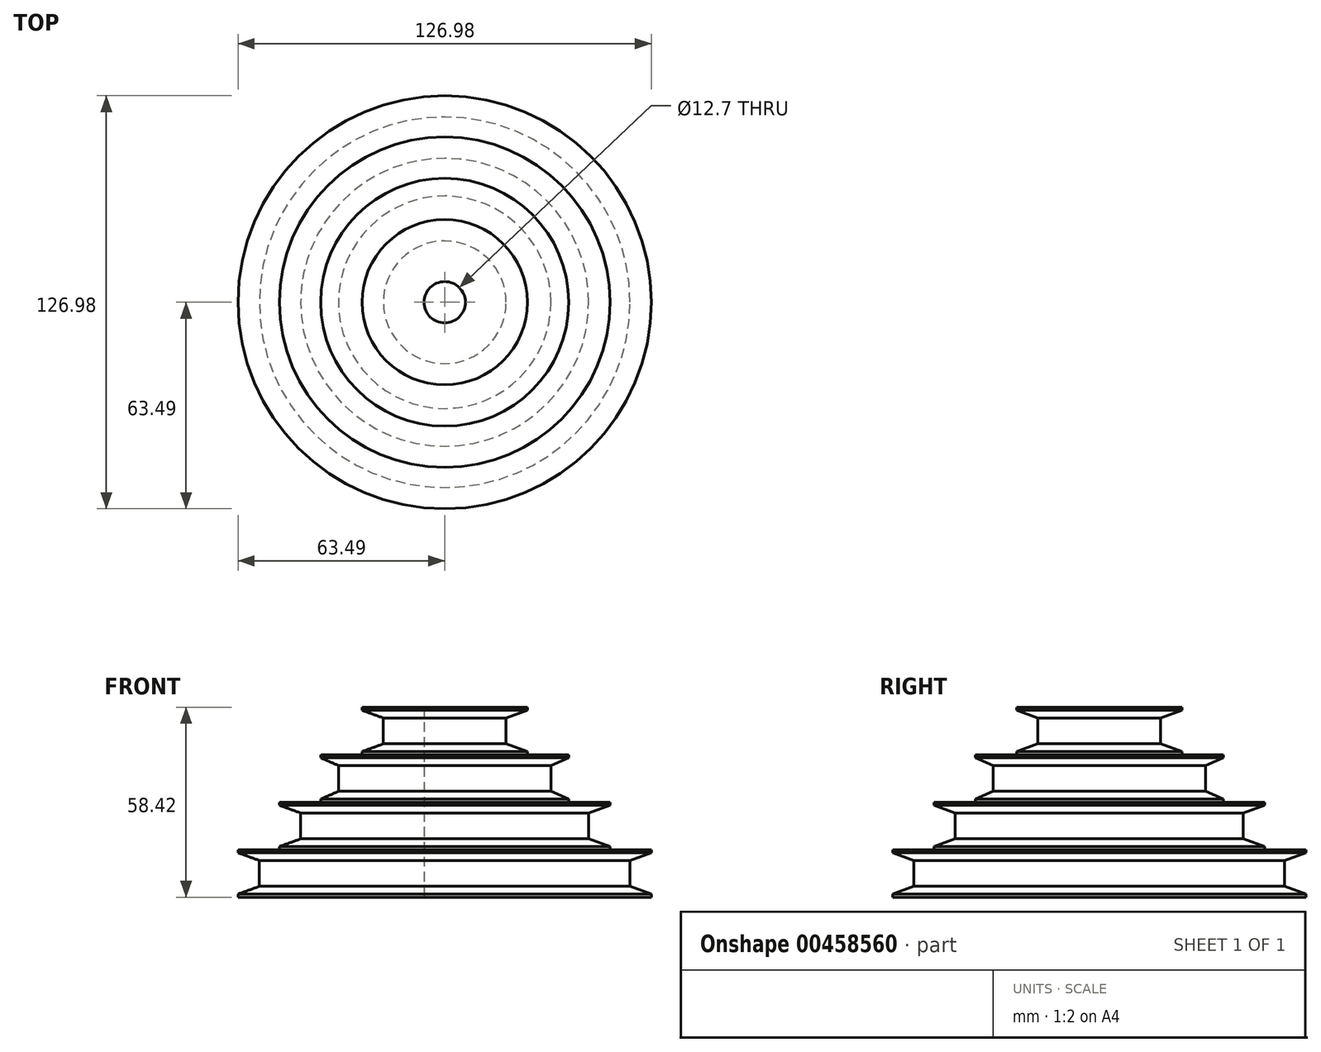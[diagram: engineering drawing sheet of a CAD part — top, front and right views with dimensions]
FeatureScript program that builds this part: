
annotation { "Feature Type Name" : "Feature", "Feature Type Description" : "" }
export const myFeature = defineFeature(function(context is Context, id is Id, definition is map)
    precondition{}
    {
        {
            var Q0;
            Q0=qCreatedBy(makeId("Front.planeOp"),FACE);
            var sketch = newSketch(context, id + "F0", { "sketchPlane" : qUnion([Q0])});
            skLineSegment(sketch, "E0", {"start": v(6.35, 58.42) * mm, "end": v(25.4, 58.42) * mm});
            skLineSegment(sketch, "E1", {"start": v(63.5, 0) * mm, "end": v(6.35, 0) * mm});
            skLineSegment(sketch, "E2.0", {"start": v(25.4, 43.81) * mm, "end": v(38.1, 43.82) * mm});
            skLineSegment(sketch, "E3.0", {"start": v(50.8, 14.6) * mm, "end": v(63.5, 14.6) * mm});
            skLineSegment(sketch, "E4", {"start": v(25.4, 58.42) * mm, "end": v(25.4, 43.82) * mm, "construction": true});
            skLineSegment(sketch, "E5", {"start": v(25.4, 51.12) * mm, "end": v(18.86, 51.12) * mm, "construction": true});
            skLineSegment(sketch, "E6", {"start": v(18.86, 51.12) * mm, "end": v(18.86, 55.09) * mm});
            skLineSegment(sketch, "E7", {"start": v(18.86, 55.09) * mm, "end": v(25.4, 57.47) * mm});
            skLineSegment(sketch, "E8", {"start": v(25.4, 57.47) * mm, "end": v(25.4, 58.42) * mm});
            skLineSegment(sketch, "E9.MirrorCS", {"start": v(18.86, 47.15) * mm, "end": v(25.4, 44.77) * mm});
            skLineSegment(sketch, "E10.MirrorCS", {"start": v(18.86, 51.12) * mm, "end": v(18.86, 47.15) * mm});
            skLineSegment(sketch, "E11", {"start": v(25.4, 44.77) * mm, "end": v(25.4, 43.82) * mm});
            skLineSegment(sketch, "E12", {"start": v(38.13, 36.51) * mm, "end": v(32.66, 36.51) * mm, "construction": true});
            skLineSegment(sketch, "E13", {"start": v(32.66, 36.51) * mm, "end": v(32.66, 40.48) * mm});
            skLineSegment(sketch, "E14", {"start": v(32.66, 40.48) * mm, "end": v(38.1, 42.86) * mm});
            skLineSegment(sketch, "E15", {"start": v(38.1, 42.86) * mm, "end": v(38.1, 43.82) * mm});
            skLineSegment(sketch, "E16", {"start": v(50.8, 21.9) * mm, "end": v(44.26, 21.9) * mm, "construction": true});
            skLineSegment(sketch, "E17", {"start": v(44.26, 21.9) * mm, "end": v(44.26, 25.88) * mm});
            skLineSegment(sketch, "E18", {"start": v(44.26, 25.88) * mm, "end": v(50.8, 28.26) * mm});
            skLineSegment(sketch, "E19", {"start": v(50.8, 28.26) * mm, "end": v(50.8, 29.21) * mm});
            skLineSegment(sketch, "E20", {"start": v(63.5, 7.3) * mm, "end": v(56.95, 7.3) * mm, "construction": true});
            skLineSegment(sketch, "E21", {"start": v(56.95, 7.3) * mm, "end": v(56.95, 11.27) * mm});
            skLineSegment(sketch, "E22", {"start": v(56.95, 11.27) * mm, "end": v(63.5, 13.65) * mm});
            skLineSegment(sketch, "E23", {"start": v(63.5, 13.65) * mm, "end": v(63.5, 14.6) * mm});
            skLineSegment(sketch, "E24.MirrorCS", {"start": v(38.1, 30.16) * mm, "end": v(38.1, 29.21) * mm});
            skLineSegment(sketch, "E25.MirrorCS", {"start": v(32.66, 32.54) * mm, "end": v(38.1, 30.16) * mm});
            skLineSegment(sketch, "E26.MirrorCS", {"start": v(32.66, 36.51) * mm, "end": v(32.66, 32.54) * mm});
            skLineSegment(sketch, "E27.MirrorCS", {"start": v(50.8, 15.56) * mm, "end": v(50.8, 14.6) * mm});
            skLineSegment(sketch, "E28.MirrorCS", {"start": v(44.26, 21.9) * mm, "end": v(44.26, 17.94) * mm});
            skLineSegment(sketch, "E29.MirrorCS", {"start": v(44.26, 17.94) * mm, "end": v(50.8, 15.56) * mm});
            skLineSegment(sketch, "E30.MirrorCS", {"start": v(63.5, 0.95) * mm, "end": v(63.5, 0) * mm});
            skLineSegment(sketch, "E31.MirrorCS", {"start": v(56.95, 7.3) * mm, "end": v(56.95, 3.33) * mm});
            skLineSegment(sketch, "E32.MirrorCS", {"start": v(56.95, 3.33) * mm, "end": v(63.5, 0.95) * mm});
            skPoint(sketch, "E33.orphan", {"position": v(0, 14.6) * mm});
            skLineSegment(sketch, "E34", {"start": v(38.1, 29.21) * mm, "end": v(50.8, 29.21) * mm});
            skLineSegment(sketch, "E35", {"start": v(38.1, 30.16) * mm, "end": v(38.1, 42.86) * mm, "construction": true});
            skLineSegment(sketch, "E36", {"start": v(6.35, 58.42) * mm, "end": v(6.35, 0) * mm});
            skLineSegment(sketch, "E37", {"start": v(0, 0) * mm, "end": v(0, 54.23) * mm, "construction": true});
            skSolve(sketch);
        }
        {
            var Q0;
            Q0 = qSketchRegion(id + "F0", true);
            var Q1;
            Q1=sQuery(id+"F0.wireOp",EDGE,"E37");
            revolve(context, id + "F1", {"surfaceOperationType" : NewSurfaceOperationType.NEW, "entities" : qUnion([Q0]), "axis" : qUnion([Q1]), "revolveType" : RevolveType.FULL});
        }
    });
